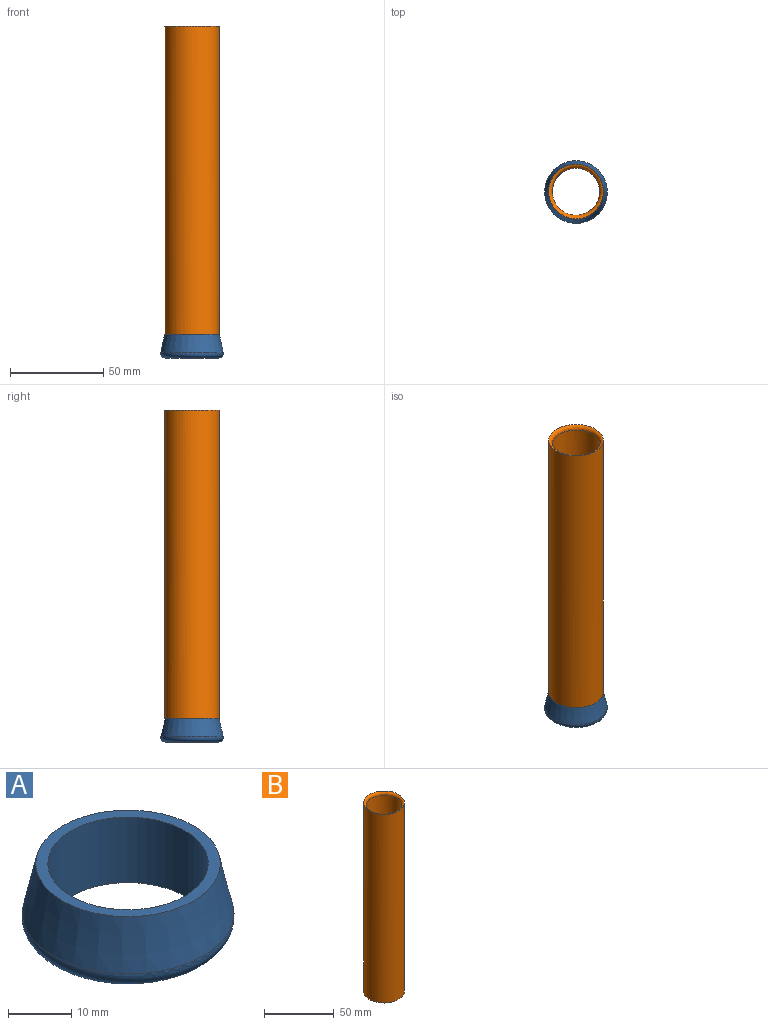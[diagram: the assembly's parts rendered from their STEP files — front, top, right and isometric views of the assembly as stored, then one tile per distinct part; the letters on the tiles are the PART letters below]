
ASSEMBLY  parts=2 mates=1
PART A: 5 faces, bbox 36.3x36.3x12.7 mm
  f0: cylinder r=12.7mm len=25.4mm, axis (0,0,-1), area 1013.4mm2, adj f1,f3
  f1: plane 28.5x28.5mm, normal (0,0,-1), area 131.1mm2, adj f0,f4
  f2: cone r=14.61mm half-angle=12.5deg, axis (0,0,-1), area 969mm2, adj f3,f4
  f3: plane 29.21x29.21mm, normal (0,0,1), area 163.4mm2, adj f0,f2
  f4: torus R=14.25mm, axis (0,0,1), area 456mm2, adj f1,f2
PART B: 4 faces, bbox 29.2x29.2x165.1 mm
  f0: cylinder r=14.61mm len=165.1mm, axis (0,0,-1), area 15150.6mm2, adj f1,f3
  f1: plane 29.21x29.21mm, normal (0,0,-1), area 163.4mm2, adj f0,f2
  f2: cylinder r=12.7mm len=162.64mm, axis (0,0,-1), area 12978.1mm2, adj f1,f3
  f3: bspline ~29.21x29.21mm, area 285mm2, adj f0,f2
PLACE A t=(-50.5,21.77,-20.56)mm
PLACE B t=(-63.2,21.77,-7.86)mm
MATE fastened A.f0 <-> B.f2  axis (0,0,-1) through (-63.2,21.77,-7.86)mm
